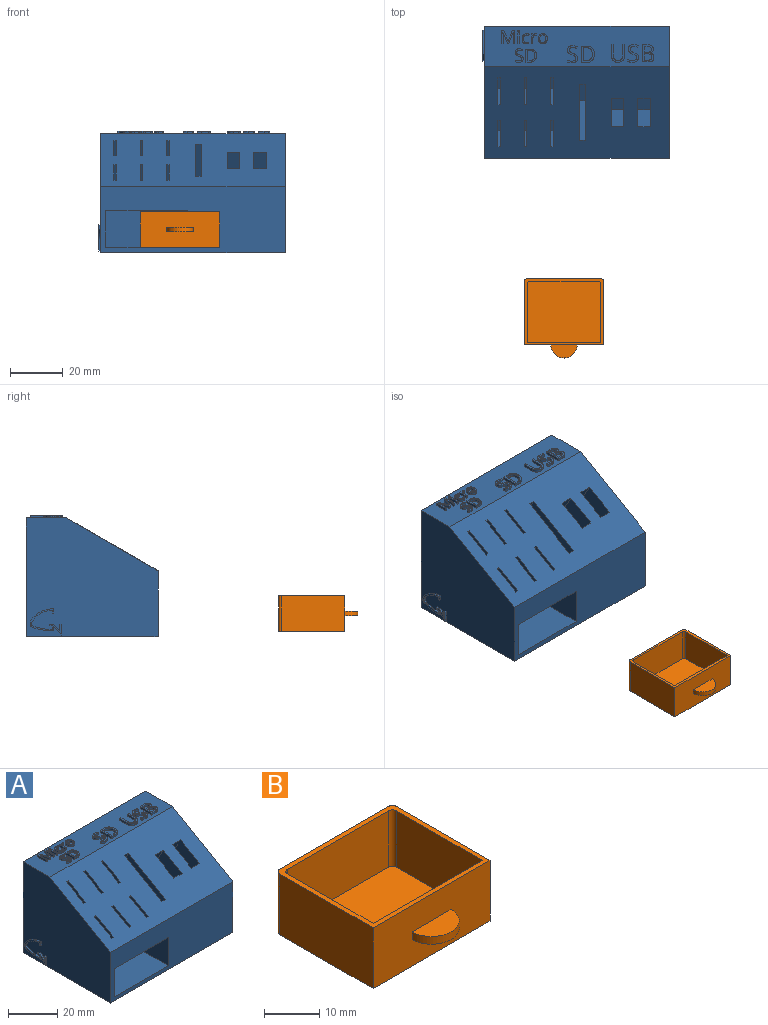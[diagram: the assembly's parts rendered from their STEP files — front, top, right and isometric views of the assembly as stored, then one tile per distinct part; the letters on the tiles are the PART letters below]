
ASSEMBLY  parts=2 mates=1
PART A: 308 faces, bbox 70.7x50x46 mm
  f0: plane 70x25mm, normal (0,-1,0), area 1316mm2, adj f1,f3,f5,f6,f303,f304,f305,f306
  f1: plane 70x34.64mm, normal (0,-0.5,0.87), area 2559.9mm2, adj f0,f2,f3,f5,f7,f8,f9,f10
  f2: plane 70x15.36mm, normal (0,0,1), area 937.8mm2, adj f1,f3,f4,f5,f47,f48,f49,f50
  f3: plane 50x45mm, normal (1,0,0), area 1903.6mm2, adj f0,f1,f2,f4,f6
  f4: plane 70x45mm, normal (0,1,0), area 3150mm2, adj f2,f3,f5,f6
  f5: plane 50x45mm, normal (-1,0,0), area 1885.7mm2, adj f0,f1,f2,f4,f6,f287,f288,f289
  f6: plane 70x50mm, normal (0,0,-1), area 3500mm2, adj f0,f3,f4,f5
  f7: plane 10.39x6mm, normal (0,0.87,0.5), area 12mm2, adj f1,f8,f10,f11
  f8: plane 16.19x16.05mm, normal (-1,0,0), area 139.2mm2, adj f1,f7,f9,f11
  f9: plane 10.39x6mm, normal (0,-0.87,-0.5), area 12mm2, adj f1,f8,f10,f11
  f10: plane 16.19x16.05mm, normal (1,0,0), area 139.2mm2, adj f1,f7,f9,f11
  f11: plane 10.05x5.8mm, normal (0,-0.5,0.87), area 11.6mm2, adj f7,f8,f9,f10
  f12: plane 10.39x6mm, normal (0,-0.87,-0.5), area 12mm2, adj f1,f13,f15,f16
  f13: plane 16.19x16.05mm, normal (1,0,0), area 139.2mm2, adj f1,f12,f14,f16
  f14: plane 10.39x6mm, normal (0,0.87,0.5), area 12mm2, adj f1,f13,f15,f16
  f15: plane 16.19x16.05mm, normal (-1,0,0), area 139.2mm2, adj f1,f12,f14,f16
  f16: plane 10.05x5.8mm, normal (0,-0.5,0.87), area 11.6mm2, adj f12,f13,f14,f15
  f17: plane 10.39x6mm, normal (0,-0.87,-0.5), area 12mm2, adj f1,f18,f20,f21
  f18: plane 16.19x16.05mm, normal (1,0,0), area 139.2mm2, adj f1,f17,f19,f21
  f19: plane 10.39x6mm, normal (0,0.87,0.5), area 12mm2, adj f1,f18,f20,f21
  f20: plane 16.19x16.05mm, normal (-1,0,0), area 139.2mm2, adj f1,f17,f19,f21
  f21: plane 10.05x5.8mm, normal (0,-0.5,0.87), area 11.6mm2, adj f17,f18,f19,f20
  f22: plane 10.39x6mm, normal (0,0.87,0.5), area 12mm2, adj f1,f23,f25,f26
  f23: plane 16.19x16.05mm, normal (-1,0,0), area 139.2mm2, adj f1,f22,f24,f26
  f24: plane 10.39x6mm, normal (0,-0.87,-0.5), area 12mm2, adj f1,f23,f25,f26
  f25: plane 16.19x16.05mm, normal (1,0,0), area 139.2mm2, adj f1,f22,f24,f26
  f26: plane 10.05x5.8mm, normal (0,-0.5,0.87), area 11.6mm2, adj f22,f23,f24,f25
  f27: plane 10.39x6mm, normal (0,-0.87,-0.5), area 12mm2, adj f1,f28,f30,f31
  f28: plane 16.19x16.05mm, normal (1,0,0), area 139.2mm2, adj f1,f27,f29,f31
  f29: plane 10.39x6mm, normal (0,0.87,0.5), area 12mm2, adj f1,f28,f30,f31
  f30: plane 16.19x16.05mm, normal (-1,0,0), area 139.2mm2, adj f1,f27,f29,f31
  f31: plane 10.05x5.8mm, normal (0,-0.5,0.87), area 11.6mm2, adj f27,f28,f29,f30
  f32: plane 10.39x6mm, normal (0,0.87,0.5), area 12mm2, adj f1,f33,f35,f36
  f33: plane 16.19x16.05mm, normal (-1,0,0), area 139.2mm2, adj f1,f32,f34,f36
  f34: plane 10.39x6mm, normal (0,-0.87,-0.5), area 12mm2, adj f1,f33,f35,f36
  f35: plane 16.19x16.05mm, normal (1,0,0), area 139.2mm2, adj f1,f32,f34,f36
  f36: plane 10.05x5.8mm, normal (0,-0.5,0.87), area 11.6mm2, adj f32,f33,f34,f35
  f37: plane 11.26x6.5mm, normal (0,-0.87,-0.5), area 61.1mm2, adj f1,f38,f40,f41
  f38: plane 17.46x17.24mm, normal (1,0,0), area 161.2mm2, adj f1,f37,f39,f41
  f39: plane 11.26x6.5mm, normal (0,0.87,0.5), area 61.1mm2, adj f1,f38,f40,f41
  f40: plane 17.46x17.24mm, normal (-1,0,0), area 161.2mm2, adj f1,f37,f39,f41
  f41: plane 10.74x6.2mm, normal (0,-0.5,0.87), area 58.3mm2, adj f37,f38,f39,f40
  f42: plane 11.26x6.5mm, normal (0,-0.87,-0.5), area 61.1mm2, adj f1,f43,f45,f46
  f43: plane 17.46x17.24mm, normal (1,0,0), area 161.2mm2, adj f1,f42,f44,f46
  f44: plane 11.26x6.5mm, normal (0,0.87,0.5), area 61.1mm2, adj f1,f43,f45,f46
  f45: plane 17.46x17.24mm, normal (-1,0,0), area 161.2mm2, adj f1,f42,f44,f46
  f46: plane 10.74x6.2mm, normal (0,-0.5,0.87), area 58.3mm2, adj f42,f43,f44,f45
  f47: plane 4.39x1.68mm, normal (-0.93,-0.36,0), area 4.7mm2, adj f2,f48,f64,f65
  f48: plane 1x0.46mm, normal (0,-1,0), area 0.5mm2, adj f2,f47,f49,f65
  f49: plane 4.39x1.7mm, normal (0.93,-0.36,0), area 4.7mm2, adj f2,f48,f50,f65
  f50: plane 1x0.03mm, normal (0,-1,0), area 0mm2, adj f2,f49,f51,f65
  f51: extruded ~1.19x1mm, area 1.2mm2, adj f2,f50,f52,f65
  f52: plane 3.19x1mm, normal (-1,0,0), area 3.2mm2, adj f2,f51,f53,f65
  f53: plane 1x0.58mm, normal (0,-1,0), area 0.6mm2, adj f2,f52,f54,f65
  f54: plane 4.96x1mm, normal (1,0,0), area 5mm2, adj f2,f53,f55,f65
  f55: plane 1x0.86mm, normal (0,1,0), area 0.9mm2, adj f2,f54,f56,f65
  f56: plane 4.09x1.58mm, normal (-0.93,0.36,0), area 4.4mm2, adj f2,f55,f57,f65
  f57: plane 1x0.03mm, normal (0,1,0), area 0mm2, adj f2,f56,f58,f65
  f58: plane 4.09x1.57mm, normal (0.93,0.36,0), area 4.4mm2, adj f2,f57,f59,f65
  f59: plane 1x0.87mm, normal (0,1,0), area 0.9mm2, adj f2,f58,f60,f65
  f60: plane 4.96x1mm, normal (-1,0,0), area 5mm2, adj f2,f59,f61,f65
  f61: plane 1x0.53mm, normal (0,-1,0), area 0.5mm2, adj f2,f60,f62,f65
  f62: plane 3.15x1mm, normal (1,0,0), area 3.2mm2, adj f2,f61,f63,f65
  f63: extruded ~1.24x1mm, area 1.2mm2, adj f2,f62,f64,f65
  f64: plane 1x0.03mm, normal (0,-1,0), area 0mm2, adj f2,f47,f63,f65
  f65: plane 4.96x4.91mm, normal (0,0,1), area 10.5mm2, adj f47,f48,f49,f50,f51,f52,f53,f54
  f66: plane 1x0.56mm, normal (0,-1,0), area 0.6mm2, adj f2,f67,f69,f70
  f67: plane 3.72x1mm, normal (1,0,0), area 3.7mm2, adj f2,f66,f68,f70
  f68: plane 1x0.56mm, normal (0,1,0), area 0.6mm2, adj f2,f67,f69,f70
  f69: plane 3.72x1mm, normal (-1,0,0), area 3.7mm2, adj f2,f66,f68,f70
  f70: plane 3.72x0.56mm, normal (0,0,1), area 2.1mm2, adj f66,f67,f68,f69
  f71: extruded ~1x0.28mm, area 0.3mm2, adj f2,f72,f78,f79
  f72: extruded ~1x0.28mm, area 0.3mm2, adj f2,f71,f73,f79
  f73: extruded ~1x0.24mm, area 0.3mm2, adj f2,f72,f74,f79
  f74: extruded ~1x0.23mm, area 0.3mm2, adj f2,f73,f75,f79
  f75: extruded ~1x0.28mm, area 0.3mm2, adj f2,f74,f76,f79
  f76: extruded ~1x0.28mm, area 0.3mm2, adj f2,f75,f77,f79
  f77: extruded ~1x0.23mm, area 0.3mm2, adj f2,f76,f78,f79
  f78: extruded ~1x0.24mm, area 0.3mm2, adj f2,f71,f77,f79
  f79: plane 0.75x0.67mm, normal (0,0,1), area 0.4mm2, adj f71,f72,f73,f74,f75,f76,f77,f78
  f80: extruded ~1.25x1mm, area 1.4mm2, adj f2,f81,f94,f95
  f81: extruded ~1x0.94mm, area 1mm2, adj f2,f80,f82,f95
  f82: plane 1x0.5mm, normal (1,0,0), area 0.5mm2, adj f2,f81,f83,f95
  f83: extruded ~1x0.95mm, area 1mm2, adj f2,f82,f84,f95
  f84: extruded ~1x0.82mm, area 0.9mm2, adj f2,f83,f85,f95
  f85: extruded ~1.05x1mm, area 1.1mm2, adj f2,f84,f86,f95
  f86: extruded ~1.44x1.13mm, area 2.1mm2, adj f2,f85,f87,f95
  f87: extruded ~1x0.39mm, area 0.4mm2, adj f2,f86,f88,f95
  f88: extruded ~1x0.41mm, area 0.4mm2, adj f2,f87,f89,f95
  f89: plane 1x0.48mm, normal (0.94,-0.34,0), area 0.5mm2, adj f2,f88,f90,f95
  f90: extruded ~1x0.42mm, area 0.4mm2, adj f2,f89,f91,f95
  f91: extruded ~1x0.54mm, area 0.5mm2, adj f2,f90,f92,f95
  f92: extruded ~1.28x1mm, area 1.4mm2, adj f2,f91,f93,f95
  f93: extruded ~1.44x1mm, area 1.5mm2, adj f2,f92,f94,f95
  f94: extruded ~1.41x1mm, area 1.5mm2, adj f2,f80,f93,f95
  f95: plane 3.85x2.69mm, normal (0,0,1), area 3.7mm2, adj f80,f81,f82,f83,f84,f85,f86,f87
  f96: extruded ~1x0.44mm, area 0.4mm2, adj f2,f97,f108,f109
  f97: extruded ~1x0.64mm, area 0.7mm2, adj f2,f96,f98,f109
  f98: extruded ~1x0.56mm, area 0.8mm2, adj f2,f97,f99,f109
  f99: plane 1x0.03mm, normal (0,1,0), area 0mm2, adj f2,f98,f100,f109
  f100: plane 1x0.69mm, normal (1,0.09,0), area 0.7mm2, adj f2,f99,f101,f109
  f101: plane 1x0.46mm, normal (0,1,0), area 0.5mm2, adj f2,f100,f102,f109
  f102: plane 3.72x1mm, normal (-1,0,0), area 3.7mm2, adj f2,f101,f103,f109
  f103: plane 1x0.56mm, normal (0,-1,0), area 0.6mm2, adj f2,f102,f104,f109
  f104: plane 1.99x1mm, normal (1,0,0), area 2mm2, adj f2,f103,f105,f109
  f105: extruded ~1x0.91mm, area 1mm2, adj f2,f104,f106,f109
  f106: extruded ~1x0.77mm, area 0.9mm2, adj f2,f105,f107,f109
  f107: extruded ~1x0.41mm, area 0.4mm2, adj f2,f106,f108,f109
  f108: plane 1x0.52mm, normal (0.99,-0.15,0), area 0.5mm2, adj f2,f96,f107,f109
  f109: plane 3.78x2.14mm, normal (0,0,1), area 2.9mm2, adj f96,f97,f98,f99,f100,f101,f102,f103
  f110: extruded ~1.09x1mm, area 1.1mm2, adj f111,f126,f127,f128
  f111: extruded ~1.08x1mm, area 1.1mm2, adj f110,f112,f127,f128
  f112: extruded ~1x0.83mm, area 0.9mm2, adj f111,f113,f127,f128
  f113: extruded ~1x0.85mm, area 1mm2, adj f112,f114,f127,f128
  f114: extruded ~1.08x1mm, area 1.1mm2, adj f113,f115,f127,f128
  f115: extruded ~1.09x1mm, area 1.1mm2, adj f114,f116,f127,f128
  f116: extruded ~1x0.84mm, area 1mm2, adj f115,f126,f127,f128
  f117: extruded ~1.42x1mm, area 1.5mm2, adj f2,f118,f125,f127
  f118: extruded ~1.4x1mm, area 1.5mm2, adj f2,f117,f119,f127
  f119: extruded ~1.24x1mm, area 1.4mm2, adj f2,f118,f120,f127
  f120: extruded ~1.26x1mm, area 1.4mm2, adj f2,f119,f121,f127
  f121: extruded ~1.42x1mm, area 1.5mm2, adj f2,f120,f122,f127
  f122: extruded ~1.02x1mm, area 1.1mm2, adj f2,f121,f123,f127
  f123: extruded ~1x0.67mm, area 0.9mm2, adj f2,f122,f124,f127
  f124: extruded ~1x0.89mm, area 0.9mm2, adj f2,f123,f125,f127
  f125: extruded ~1.26x1mm, area 1.4mm2, adj f2,f117,f124,f127
  f126: extruded ~1x0.84mm, area 1mm2, adj f110,f116,f127,f128
  f127: plane 3.85x3.41mm, normal (0,0,1), area 5.3mm2, adj f110,f111,f112,f113,f114,f115,f116,f117
  f128: plane 2.9x2.25mm, normal (0,0,1), area 5.4mm2, adj f110,f111,f112,f113,f114,f115,f116,f126
  f129: extruded ~1.02x1mm, area 1.2mm2, adj f2,f130,f153,f154
  f130: extruded ~1x0.83mm, area 0.9mm2, adj f2,f129,f131,f154
  f131: extruded ~1.07x1mm, area 1.2mm2, adj f2,f130,f132,f154
  f132: extruded ~1x0.69mm, area 0.8mm2, adj f2,f131,f133,f154
  f133: extruded ~1x0.32mm, area 0.4mm2, adj f2,f132,f134,f154
  f134: extruded ~1x0.42mm, area 0.4mm2, adj f2,f133,f135,f154
  f135: extruded ~1x0.55mm, area 0.6mm2, adj f2,f134,f136,f154
  f136: extruded ~1x0.72mm, area 0.8mm2, adj f2,f135,f137,f154
  f137: extruded ~1.19x1mm, area 1.2mm2, adj f2,f136,f138,f154
  f138: plane 1x0.5mm, normal (0.94,-0.34,0), area 0.5mm2, adj f2,f137,f139,f154
  f139: extruded ~1.36x1mm, area 1.4mm2, adj f2,f138,f140,f154
  f140: extruded ~1.14x1mm, area 1.2mm2, adj f2,f139,f141,f154
  f141: extruded ~1x0.91mm, area 1mm2, adj f2,f140,f142,f154
  f142: extruded ~1x0.89mm, area 1mm2, adj f2,f141,f143,f154
  f143: extruded ~1x0.99mm, area 1.2mm2, adj f2,f142,f144,f154
  f144: extruded ~1x0.74mm, area 0.8mm2, adj f2,f143,f145,f154
  f145: extruded ~1x0.35mm, area 0.5mm2, adj f2,f144,f146,f154
  f146: extruded ~1x0.42mm, area 0.4mm2, adj f2,f145,f147,f154
  f147: extruded ~1x0.61mm, area 0.7mm2, adj f2,f146,f148,f154
  f148: extruded ~1x0.87mm, area 0.9mm2, adj f2,f147,f149,f154
  f149: extruded ~1x0.71mm, area 0.7mm2, adj f2,f148,f150,f154
  f150: extruded ~1x0.67mm, area 0.7mm2, adj f2,f149,f151,f154
  f151: plane 1x0.56mm, normal (-1,0,0), area 0.6mm2, adj f2,f150,f152,f154
  f152: extruded ~1.36x1mm, area 1.4mm2, adj f2,f151,f153,f154
  f153: extruded ~1.29x1mm, area 1.4mm2, adj f2,f129,f152,f154
  f154: plane 5.1x3.12mm, normal (0,0,1), area 5.7mm2, adj f129,f130,f131,f132,f133,f134,f135,f136
  f155: extruded ~1.46x1mm, area 1.6mm2, adj f156,f168,f169,f170
  f156: extruded ~1.5x1mm, area 1.6mm2, adj f155,f157,f169,f170
  f157: extruded ~1.55x1mm, area 1.7mm2, adj f156,f158,f169,f170
  f158: plane 1x0.7mm, normal (0,1,0), area 0.7mm2, adj f157,f159,f169,f170
  f159: plane 3.96x1mm, normal (1,0,0), area 4mm2, adj f158,f160,f169,f170
  f160: plane 1x0.84mm, normal (0,-1,0), area 0.8mm2, adj f159,f168,f169,f170
  f161: extruded ~1.88x1mm, area 2mm2, adj f2,f162,f167,f169
  f162: extruded ~1.79x1mm, area 2mm2, adj f2,f161,f163,f169
  f163: extruded ~1.8x1mm, area 2mm2, adj f2,f162,f164,f169
  f164: plane 1.52x1mm, normal (0,1,0), area 1.5mm2, adj f2,f163,f165,f169
  f165: plane 4.96x1mm, normal (-1,0,0), area 5mm2, adj f2,f164,f166,f169
  f166: plane 1.37x1mm, normal (0,-1,0), area 1.4mm2, adj f2,f165,f167,f169
  f167: extruded ~1.92x1mm, area 2.1mm2, adj f2,f161,f166,f169
  f168: extruded ~1.45x1mm, area 1.6mm2, adj f155,f160,f169,f170
  f169: plane 4.96x3.96mm, normal (0,0,1), area 7.8mm2, adj f155,f156,f157,f158,f159,f160,f161,f162
  f170: plane 3.96x2.77mm, normal (0,0,1), area 9.6mm2, adj f155,f156,f157,f158,f159,f160,f168
  f171: extruded ~1.29x1mm, area 1.5mm2, adj f2,f172,f195,f196
  f172: extruded ~1.05x1mm, area 1.1mm2, adj f2,f171,f173,f196
  f173: extruded ~1.36x1mm, area 1.6mm2, adj f2,f172,f174,f196
  f174: extruded ~1x0.88mm, area 1mm2, adj f2,f173,f175,f196
  f175: extruded ~1x0.41mm, area 0.6mm2, adj f2,f174,f176,f196
  f176: extruded ~1x0.54mm, area 0.6mm2, adj f2,f175,f177,f196
  f177: extruded ~1x0.69mm, area 0.8mm2, adj f2,f176,f178,f196
  f178: extruded ~1x0.91mm, area 1mm2, adj f2,f177,f179,f196
  f179: extruded ~1.51x1mm, area 1.6mm2, adj f2,f178,f180,f196
  f180: plane 1x0.64mm, normal (0.94,-0.34,0), area 0.7mm2, adj f2,f179,f181,f196
  f181: extruded ~1.72x1mm, area 1.8mm2, adj f2,f180,f182,f196
  f182: extruded ~1.45x1mm, area 1.5mm2, adj f2,f181,f183,f196
  f183: extruded ~1.16x1mm, area 1.3mm2, adj f2,f182,f184,f196
  f184: extruded ~1.12x1mm, area 1.2mm2, adj f2,f183,f185,f196
  f185: extruded ~1.25x1mm, area 1.5mm2, adj f2,f184,f186,f196
  f186: extruded ~1x0.93mm, area 1mm2, adj f2,f185,f187,f196
  f187: extruded ~1x0.44mm, area 0.6mm2, adj f2,f186,f188,f196
  f188: extruded ~1x0.53mm, area 0.6mm2, adj f2,f187,f189,f196
  f189: extruded ~1x0.77mm, area 0.9mm2, adj f2,f188,f190,f196
  f190: extruded ~1.1x1mm, area 1.2mm2, adj f2,f189,f191,f196
  f191: extruded ~1x0.9mm, area 0.9mm2, adj f2,f190,f192,f196
  f192: extruded ~1x0.84mm, area 0.9mm2, adj f2,f191,f193,f196
  f193: plane 1x0.7mm, normal (-1,0,0), area 0.7mm2, adj f2,f192,f194,f196
  f194: extruded ~1.72x1mm, area 1.8mm2, adj f2,f193,f195,f196
  f195: extruded ~1.63x1mm, area 1.7mm2, adj f2,f171,f194,f196
  f196: plane 6.46x3.95mm, normal (0,0,1), area 9.1mm2, adj f171,f172,f173,f174,f175,f176,f177,f178
  f197: extruded ~1.85x1mm, area 2mm2, adj f198,f210,f211,f212
  f198: extruded ~1.9x1mm, area 2.1mm2, adj f197,f199,f211,f212
  f199: extruded ~1.97x1mm, area 2.1mm2, adj f198,f200,f211,f212
  f200: plane 1x0.89mm, normal (0,1,0), area 0.9mm2, adj f199,f201,f211,f212
  f201: plane 5.02x1mm, normal (1,0,0), area 5mm2, adj f200,f202,f211,f212
  f202: plane 1.06x1mm, normal (0,-1,0), area 1.1mm2, adj f201,f210,f211,f212
  f203: extruded ~2.38x1mm, area 2.6mm2, adj f2,f204,f209,f211
  f204: extruded ~2.27x1mm, area 2.5mm2, adj f2,f203,f205,f211
  f205: extruded ~2.28x1mm, area 2.5mm2, adj f2,f204,f206,f211
  f206: plane 1.93x1mm, normal (0,1,0), area 1.9mm2, adj f2,f205,f207,f211
  f207: plane 6.28x1mm, normal (-1,0,0), area 6.3mm2, adj f2,f206,f208,f211
  f208: plane 1.74x1mm, normal (0,-1,0), area 1.7mm2, adj f2,f207,f209,f211
  f209: extruded ~2.43x1mm, area 2.6mm2, adj f2,f203,f208,f211
  f210: extruded ~1.83x1mm, area 2mm2, adj f197,f202,f211,f212
  f211: plane 6.28x5.02mm, normal (0,0,1), area 12.5mm2, adj f197,f198,f199,f200,f201,f202,f203,f204
  f212: plane 5.02x3.51mm, normal (0,0,1), area 15.5mm2, adj f197,f198,f199,f200,f201,f202,f210
  f213: plane 4.19x1mm, normal (1,0,0), area 4.2mm2, adj f2,f214,f226,f227
  f214: plane 1x0.75mm, normal (0,1,0), area 0.8mm2, adj f2,f213,f215,f227
  f215: plane 4.22x1mm, normal (-1,0,0), area 4.2mm2, adj f2,f214,f216,f227
  f216: extruded ~1.25x1mm, area 1.4mm2, adj f2,f215,f217,f227
  f217: extruded ~1.26x1mm, area 1.4mm2, adj f2,f216,f218,f227
  f218: extruded ~1.3x1mm, area 1.4mm2, adj f2,f217,f219,f227
  f219: extruded ~1.25x1mm, area 1.4mm2, adj f2,f218,f220,f227
  f220: plane 4.23x1mm, normal (1,0,0), area 4.2mm2, adj f2,f219,f221,f227
  f221: plane 1x0.75mm, normal (0,1,0), area 0.8mm2, adj f2,f220,f222,f227
  f222: plane 4.17x1mm, normal (-1,0,0), area 4.2mm2, adj f2,f221,f223,f227
  f223: extruded ~1.75x1mm, area 1.9mm2, adj f2,f222,f224,f227
  f224: extruded ~1.81x1mm, area 2mm2, adj f2,f223,f225,f227
  f225: extruded ~1.84x1mm, area 2mm2, adj f2,f224,f226,f227
  f226: extruded ~1.74x1mm, area 1.9mm2, adj f2,f213,f225,f227
  f227: plane 6.57x4.96mm, normal (0,0,1), area 11mm2, adj f213,f214,f215,f216,f217,f218,f219,f220
  f228: extruded ~1.33x1mm, area 1.5mm2, adj f2,f229,f252,f253
  f229: extruded ~1.08x1mm, area 1.2mm2, adj f2,f228,f230,f253
  f230: extruded ~1.4x1mm, area 1.6mm2, adj f2,f229,f231,f253
  f231: extruded ~1x0.9mm, area 1mm2, adj f2,f230,f232,f253
  f232: extruded ~1x0.42mm, area 0.6mm2, adj f2,f231,f233,f253
  f233: extruded ~1x0.55mm, area 0.6mm2, adj f2,f232,f234,f253
  f234: extruded ~1x0.71mm, area 0.8mm2, adj f2,f233,f235,f253
  f235: extruded ~1x0.94mm, area 1mm2, adj f2,f234,f236,f253
  f236: extruded ~1.56x1mm, area 1.6mm2, adj f2,f235,f237,f253
  f237: plane 1x0.66mm, normal (0.94,-0.34,0), area 0.7mm2, adj f2,f236,f238,f253
  f238: extruded ~1.78x1mm, area 1.8mm2, adj f2,f237,f239,f253
  f239: extruded ~1.49x1mm, area 1.6mm2, adj f2,f238,f240,f253
  f240: extruded ~1.19x1mm, area 1.4mm2, adj f2,f239,f241,f253
  f241: extruded ~1.16x1mm, area 1.2mm2, adj f2,f240,f242,f253
  f242: extruded ~1.29x1mm, area 1.5mm2, adj f2,f241,f243,f253
  f243: extruded ~1x0.96mm, area 1mm2, adj f2,f242,f244,f253
  f244: extruded ~1x0.45mm, area 0.6mm2, adj f2,f243,f245,f253
  f245: extruded ~1x0.55mm, area 0.6mm2, adj f2,f244,f246,f253
  f246: extruded ~1x0.8mm, area 0.9mm2, adj f2,f245,f247,f253
  f247: extruded ~1.13x1mm, area 1.2mm2, adj f2,f246,f248,f253
  f248: extruded ~1x0.93mm, area 0.9mm2, adj f2,f247,f249,f253
  f249: extruded ~1x0.87mm, area 0.9mm2, adj f2,f248,f250,f253
  f250: plane 1x0.73mm, normal (-1,0,0), area 0.7mm2, adj f2,f249,f251,f253
  f251: extruded ~1.77x1mm, area 1.8mm2, adj f2,f250,f252,f253
  f252: extruded ~1.68x1mm, area 1.8mm2, adj f2,f228,f251,f253
  f253: plane 6.66x4.08mm, normal (0,0,1), area 9.7mm2, adj f228,f229,f230,f231,f232,f233,f234,f235
  f254: plane 2.42x1mm, normal (1,0,0), area 2.4mm2, adj f255,f278,f279,f280
  f255: plane 1.29x1mm, normal (0,-1,0), area 1.3mm2, adj f254,f256,f279,f280
  f256: extruded ~1.23x1mm, area 1.3mm2, adj f255,f257,f279,f280
  f257: extruded ~1x0.89mm, area 1mm2, adj f256,f258,f279,f280
  f258: extruded ~1x0.95mm, area 1.1mm2, adj f257,f259,f279,f280
  f259: extruded ~1.18x1mm, area 1.2mm2, adj f258,f278,f279,f280
  f260: plane 1.24x1mm, normal (0,1,0), area 1.2mm2, adj f261,f276,f279,f281
  f261: plane 2.12x1mm, normal (1,0,0), area 2.1mm2, adj f260,f262,f279,f281
  f262: plane 1.11x1mm, normal (0,-1,0), area 1.1mm2, adj f261,f263,f279,f281
  f263: extruded ~1.24x1mm, area 1.3mm2, adj f262,f264,f279,f281
  f264: extruded ~1x0.79mm, area 0.9mm2, adj f263,f265,f279,f281
  f265: extruded ~1x0.84mm, area 0.9mm2, adj f264,f276,f279,f281
  f266: plane 1.83x1mm, normal (0,1,0), area 1.8mm2, adj f2,f267,f277,f279
  f267: plane 6.48x1mm, normal (-1,0,0), area 6.5mm2, adj f2,f266,f268,f279
  f268: plane 2.26x1mm, normal (0,-1,0), area 2.3mm2, adj f2,f267,f269,f279
  f269: extruded ~1.64x1mm, area 1.7mm2, adj f2,f268,f270,f279
  f270: extruded ~1.36x1mm, area 1.5mm2, adj f2,f269,f271,f279
  f271: extruded ~1.55x1.48mm, area 2.4mm2, adj f2,f270,f272,f279
  f272: plane 1x0.04mm, normal (1,0,0), area 0mm2, adj f2,f271,f273,f279
  f273: extruded ~1x0.94mm, area 1.1mm2, adj f2,f272,f274,f279
  f274: extruded ~1x0.95mm, area 1mm2, adj f2,f273,f275,f279
  f275: extruded ~1.22x1mm, area 1.4mm2, adj f2,f274,f277,f279
  f276: extruded ~1.15x1mm, area 1.2mm2, adj f260,f265,f279,f281
  f277: extruded ~1.87x1mm, area 1.9mm2, adj f2,f266,f275,f279
  f278: plane 1.35x1mm, normal (0,1,0), area 1.4mm2, adj f254,f259,f279,f280
  f279: plane 6.48x4.49mm, normal (0,0,1), area 14.3mm2, adj f254,f255,f256,f257,f258,f259,f260,f261
  f280: plane 2.93x2.42mm, normal (0,0,1), area 6.5mm2, adj f254,f255,f256,f257,f258,f259,f278
  f281: plane 2.74x2.12mm, normal (0,0,1), area 5.3mm2, adj f260,f261,f262,f263,f264,f265,f276
  f282: plane 25.98x15mm, normal (0,-0.87,-0.5), area 66mm2, adj f1,f283,f285,f286
  f283: plane 38.23x36.22mm, normal (1,0,0), area 735mm2, adj f1,f282,f284,f286
  f284: plane 25.98x15mm, normal (0,0.87,0.5), area 66mm2, adj f1,f283,f285,f286
  f285: plane 38.23x36.22mm, normal (-1,0,0), area 735mm2, adj f1,f282,f284,f286
  f286: plane 21.22x12.25mm, normal (0,-0.5,0.87), area 53.9mm2, adj f282,f283,f284,f285
  f287: plane 1.65x0.66mm, normal (0,-1,0), area 1.1mm2, adj f5,f288,f301,f302
  f288: extruded ~9.08x8.46mm, area 14.2mm2, adj f5,f287,f289,f302
  f289: plane 1.66x0.66mm, normal (0,-1,0), area 1.1mm2, adj f5,f288,f290,f302
  f290: plane 3.19x2.71mm, normal (0,0.76,-0.65), area 2.8mm2, adj f5,f289,f291,f302
  f291: plane 4.06x0.66mm, normal (0,-1,0), area 2.7mm2, adj f5,f290,f292,f302
  f292: plane 0.66x0.56mm, normal (0,0,1), area 0.4mm2, adj f5,f291,f293,f302
  f293: plane 2.53x0.66mm, normal (0,1,0), area 1.7mm2, adj f5,f292,f294,f302
  f294: plane 2.53x2.15mm, normal (0,-0.76,0.65), area 2.2mm2, adj f5,f293,f295,f302
  f295: plane 1.65x0.66mm, normal (0,0,1), area 1.1mm2, adj f5,f294,f296,f302
  f296: plane 0.66x0.56mm, normal (0,1,0), area 0.4mm2, adj f5,f295,f297,f302
  f297: plane 1.09x0.66mm, normal (0,0,-1), area 0.7mm2, adj f5,f296,f298,f302
  f298: plane 1.41x0.66mm, normal (0,1,0), area 0.9mm2, adj f5,f297,f299,f302
  f299: extruded ~7.96x7.33mm, area 12.3mm2, adj f5,f298,f300,f302
  f300: plane 1.08x0.66mm, normal (0,1,0), area 0.7mm2, adj f5,f299,f301,f302
  f301: plane 0.66x0.56mm, normal (0,0,-1), area 0.4mm2, adj f5,f287,f300,f302
  f302: plane 12.26x10.01mm, normal (-1,0,0), area 17.9mm2, adj f287,f288,f289,f290,f291,f292,f293,f294
  f303: plane 31x25mm, normal (0,0,-1), area 775mm2, adj f0,f304,f306,f307
  f304: plane 25x14mm, normal (1,0,0), area 350mm2, adj f0,f303,f305,f307
  f305: plane 31x25mm, normal (0,0,1), area 775mm2, adj f0,f304,f306,f307
  f306: plane 25x14mm, normal (-1,0,0), area 350mm2, adj f0,f303,f305,f307
  f307: plane 31x14mm, normal (0,-1,0), area 434mm2, adj f303,f304,f305,f306
PART B: 18 faces, bbox 30x30x13.5 mm
  f0: plane 30x13.5mm, normal (0,-1,0), area 388mm2, adj f1,f2,f4,f5,f11,f12,f13
  f1: plane 30x25mm, normal (0,0,1), area 106mm2, adj f0,f2,f3,f4,f6,f7,f8,f9
  f2: plane 24x13.5mm, normal (1,0,0), area 324mm2, adj f0,f1,f5,f16
  f3: plane 28x13.5mm, normal (0,1,0), area 378mm2, adj f1,f5,f16,f17
  f4: plane 24x13.5mm, normal (-1,0,0), area 324mm2, adj f0,f1,f5,f17
  f5: plane 30x25mm, normal (0,0,-1), area 749.6mm2, adj f0,f2,f3,f4,f16,f17
  f6: plane 28x12.5mm, normal (0,1,0), area 350mm2, adj f1,f7,f9,f10
  f7: plane 22x12.5mm, normal (-1,0,0), area 275mm2, adj f1,f6,f10,f15
  f8: plane 26x12.5mm, normal (0,-1,0), area 325mm2, adj f1,f10,f14,f15
  f9: plane 22x12.5mm, normal (1,0,0), area 275mm2, adj f1,f6,f10,f14
  f10: plane 28x23mm, normal (0,0,1), area 643.6mm2, adj f6,f7,f8,f9,f14,f15
  f11: plane 10x5mm, normal (0,0,1), area 39.3mm2, adj f0,f12
  f12: cylinder r=5mm len=10mm, axis (0,0,-1), area 26.7mm2, adj f0,f11,f13
  f13: plane 10x5mm, normal (0,0,-1), area 39.3mm2, adj f0,f12
  f14: cylinder r=1mm len=12.5mm, axis (0,0,-1), area 19.6mm2, adj f1,f8,f9,f10
  f15: cylinder r=1mm len=12.5mm, axis (0,0,1), area 19.6mm2, adj f1,f7,f8,f10
  f16: cylinder r=1mm len=13.5mm, axis (0,0,-1), area 21.2mm2, adj f1,f2,f3,f5
  f17: cylinder r=1mm len=13.5mm, axis (0,0,1), area 21.2mm2, adj f1,f3,f4,f5
PLACE A t=(-8.67,-0.23,20.23)mm fixed
PLACE B t=(6.24,-99.85,22.23)mm
MATE planar A.f305 <-> B.f5  axis (0,0,1) through (-26.17,-12.73,22.23)mm
